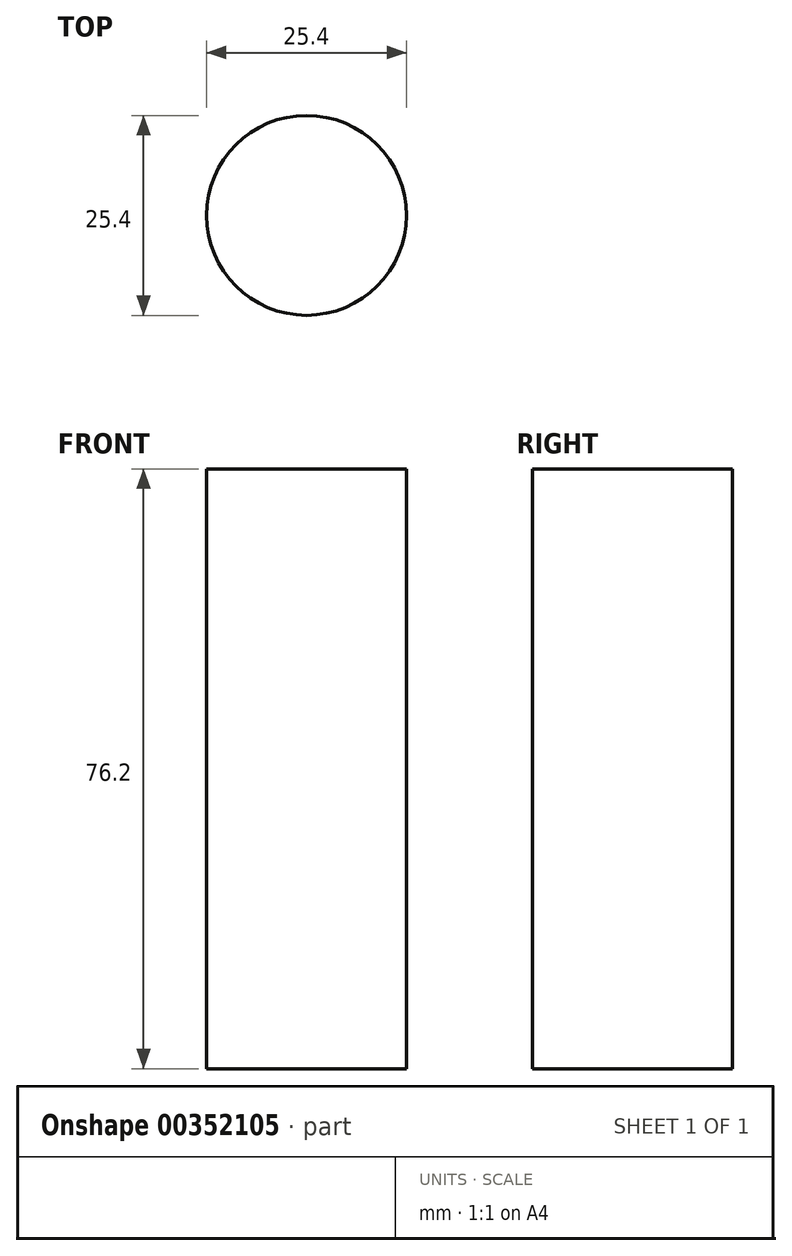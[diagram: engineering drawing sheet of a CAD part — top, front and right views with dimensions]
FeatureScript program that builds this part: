
annotation { "Feature Type Name" : "Feature", "Feature Type Description" : "" }
export const myFeature = defineFeature(function(context is Context, id is Id, definition is map)
    precondition{}
    {
        {
            var Q0;
            Q0=qCreatedBy(makeId("Top.planeOp"),FACE);
            var sketch = newSketch(context, id + "F0", { "sketchPlane" : qUnion([Q0])});
            skCircle(sketch, "E0", {"center": v(0, 0) * mm, "radius": 12.7 * mm});
            skSolve(sketch);
        }
        {
            var Q0;
            Q0=makeQuery(id+"F0.imprint","IMPRINT",FACE,{"disambiguationData":[TD([[makeQuery(id+"F0.imprint","IMPRINT",EDGE,{"derivedFrom":sQuery(id+"F0.wireOp",EDGE,"E0")}),1.0]])]});
            extrude(context, id + "F1", {"entities" : qUnion([Q0]), "depth" : 76.2 * mm});
        }
    });
